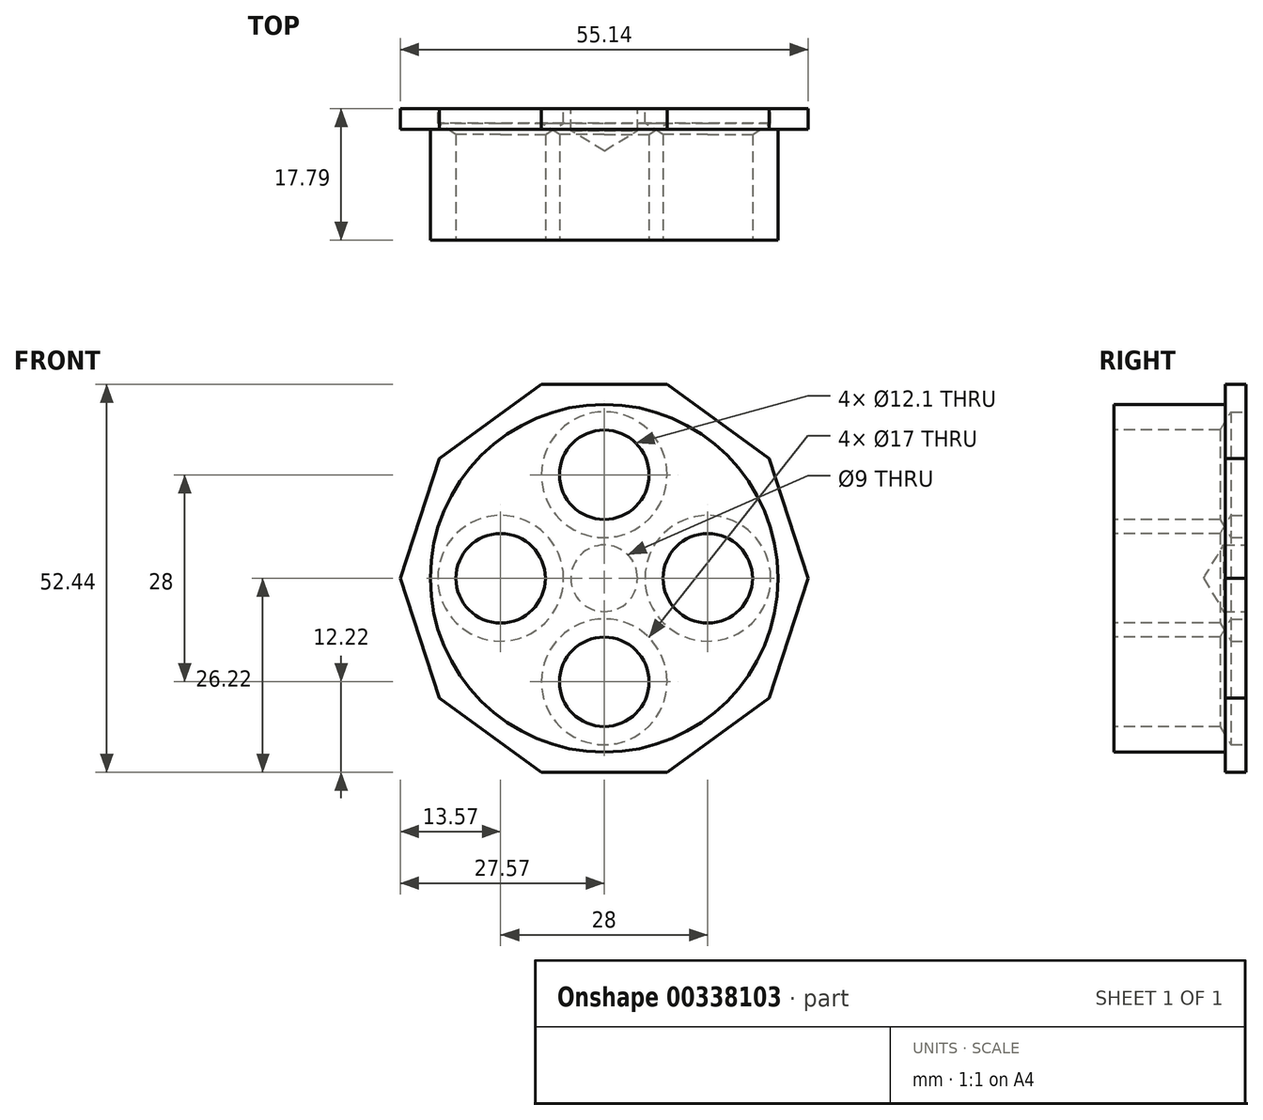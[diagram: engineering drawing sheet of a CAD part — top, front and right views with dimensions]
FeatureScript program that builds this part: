
annotation { "Feature Type Name" : "Feature", "Feature Type Description" : "" }
export const myFeature = defineFeature(function(context is Context, id is Id, definition is map)
    precondition{}
    {
        {
            var Q0;
            Q0=qCreatedBy(makeId("Front.planeOp"),FACE);
            var sketch = newSketch(context, id + "F0", { "sketchPlane" : qUnion([Q0])});
            skCircle(sketch, "E0.cCircle", {"center": v(0, 0) * mm, "radius": 27.57 * mm, "construction": true});
            skLineSegment(sketch, "E0.0", {"start": v(-27.57, 0) * mm, "end": v(-22.3, 16.2) * mm});
            skLineSegment(sketch, "E0.1", {"start": v(-22.3, 16.2) * mm, "end": v(-8.52, 26.22) * mm});
            skLineSegment(sketch, "E0.2", {"start": v(-8.52, 26.22) * mm, "end": v(8.52, 26.22) * mm});
            skLineSegment(sketch, "E0.3", {"start": v(8.52, 26.22) * mm, "end": v(22.3, 16.2) * mm});
            skLineSegment(sketch, "E0.4", {"start": v(22.3, 16.2) * mm, "end": v(27.57, 0) * mm});
            skLineSegment(sketch, "E0.5", {"start": v(27.57, 0) * mm, "end": v(22.3, -16.2) * mm});
            skLineSegment(sketch, "E0.6", {"start": v(22.3, -16.2) * mm, "end": v(8.52, -26.22) * mm});
            skLineSegment(sketch, "E0.7", {"start": v(8.52, -26.22) * mm, "end": v(-8.52, -26.22) * mm});
            skLineSegment(sketch, "E0.8", {"start": v(-8.52, -26.22) * mm, "end": v(-22.3, -16.2) * mm});
            skLineSegment(sketch, "E0.9", {"start": v(-22.3, -16.2) * mm, "end": v(-27.57, 0) * mm});
            skSolve(sketch);
        }
        {
            var Q0;
            Q0=makeQuery(id+"F0.imprint","IMPRINT",FACE,{"disambiguationData":[TD([[makeQuery(id+"F0.imprint","IMPRINT",EDGE,{"derivedFrom":sQuery(id+"F0.wireOp",EDGE,"E0.0")}),-1.0]])]});
            extrude(context, id + "F1", {"entities" : qUnion([Q0]), "depth" : 2.8 * mm});
        }
        {
            var Q0;
            Q0=makeQuery(id+"F1.opExtrude","CAP_FACE",FACE,{"disambiguationData":[OSD([sQuery(id+"F0.wireOp",EDGE,"E0.0"),sQuery(id+"F0.wireOp",EDGE,"E0.1"),sQuery(id+"F0.wireOp",EDGE,"E0.2"),sQuery(id+"F0.wireOp",EDGE,"E0.3"),sQuery(id+"F0.wireOp",EDGE,"E0.4"),sQuery(id+"F0.wireOp",EDGE,"E0.5"),sQuery(id+"F0.wireOp",EDGE,"E0.6"),sQuery(id+"F0.wireOp",EDGE,"E0.7"),sQuery(id+"F0.wireOp",EDGE,"E0.8"),sQuery(id+"F0.wireOp",EDGE,"E0.9")])],"isStart":false});
            var sketch = newSketch(context, id + "F2", { "sketchPlane" : qUnion([Q0])});
            skCircle(sketch, "E1", {"center": v(0, 0) * mm, "radius": 23.5 * mm});
            skSolve(sketch);
        }
        {
            var Q0;
            Q0=makeQuery(id+"F2.imprint","IMPRINT",FACE,{"disambiguationData":[TD([[makeQuery(id+"F2.imprint","IMPRINT",EDGE,{"derivedFrom":sQuery(id+"F2.wireOp",EDGE,"E1")}),1.0]])]});
            extrude(context, id + "F3", {"entities" : qUnion([Q0]), "operationType" : NewBodyOperationType.ADD, "depth" : 15 * mm});
        }
        {
            var Q0;
            Q0=makeQuery(id+"F3.opExtrude","CAP_FACE",FACE,{"disambiguationData":[OSD([sQuery(id+"F2.wireOp",EDGE,"E1")])],"isStart":false});
            var sketch = newSketch(context, id + "F4", { "sketchPlane" : qUnion([Q0])});
            skCircle(sketch, "E2", {"center": v(0, 14) * mm, "radius": 7 * mm});
            skCircle(sketch, "E3", {"center": v(14, 0) * mm, "radius": 7 * mm});
            skCircle(sketch, "E4", {"center": v(0, -14) * mm, "radius": 7 * mm});
            skCircle(sketch, "E5", {"center": v(-14, 0) * mm, "radius": 7 * mm});
            skSolve(sketch);
        }
        {
            var Q0;
            Q0=sQuery(id+"F4.wireOp",VERTEX,"E5.center");
            var Q1;
            Q1=sQuery(id+"F4.wireOp",VERTEX,"E2.center");
            var Q2;
            Q2=sQuery(id+"F4.wireOp",VERTEX,"E3.center");
            var Q3;
            Q3=sQuery(id+"F4.wireOp",VERTEX,"E4.center");
            var Q4;
            Q4=makeQuery(id+"F1.opExtrude","SWEPT_BODY",BODY,{"disambiguationData":[OSD([sQuery(id+"F0.wireOp",EDGE,"E0.0"),sQuery(id+"F0.wireOp",EDGE,"E0.1"),sQuery(id+"F0.wireOp",EDGE,"E0.2"),sQuery(id+"F0.wireOp",EDGE,"E0.3"),sQuery(id+"F0.wireOp",EDGE,"E0.4"),sQuery(id+"F0.wireOp",EDGE,"E0.5"),sQuery(id+"F0.wireOp",EDGE,"E0.6"),sQuery(id+"F0.wireOp",EDGE,"E0.7"),sQuery(id+"F0.wireOp",EDGE,"E0.8"),sQuery(id+"F0.wireOp",EDGE,"E0.9")])]});
            hole(context, id + "F5", {"style" : HoleStyle.SIMPLE, "endStyle" : HoleEndStyle.THROUGH, "standardTappedOrClearance" : lookupTablePath({ "standard" : "ISO", "engagement" : "75%", "pitch" : "2 mm", "size" : "M14", "type" : "Tapped" }), "standardBlindInLast" : lookupTablePath({ "standard" : "ISO", "engagement" : "75%", "pitch" : "2 mm", "size" : "M14", "type" : "Tapped" }), "holeDiameter" : 12.1 * mm, "showTappedDepth" : true, "tappedDepth" : 12 * mm, "tapClearance" : 3, "locations" : qUnion([Q0, Q1, Q2, Q3]), "scope" : qUnion([Q4]), "majorDiameter" : 14 * mm});
        }
        {
            var Q0;
            Q0=makeQuery(id+"F1.opExtrude","CAP_FACE",FACE,{"disambiguationData":[OSD([sQuery(id+"F0.wireOp",EDGE,"E0.0"),sQuery(id+"F0.wireOp",EDGE,"E0.1"),sQuery(id+"F0.wireOp",EDGE,"E0.2"),sQuery(id+"F0.wireOp",EDGE,"E0.3"),sQuery(id+"F0.wireOp",EDGE,"E0.4"),sQuery(id+"F0.wireOp",EDGE,"E0.5"),sQuery(id+"F0.wireOp",EDGE,"E0.6"),sQuery(id+"F0.wireOp",EDGE,"E0.7"),sQuery(id+"F0.wireOp",EDGE,"E0.8"),sQuery(id+"F0.wireOp",EDGE,"E0.9")])],"isStart":true});
            var sketch = newSketch(context, id + "F6", { "sketchPlane" : qUnion([Q0])});
            skCircle(sketch, "E6", {"center": v(0, 0) * mm, "radius": 4.5 * mm});
            skSolve(sketch);
        }
        {
            var Q0;
            Q0=sQuery(id+"F6.wireOp",VERTEX,"E6.center");
            var Q1;
            Q1=makeQuery(id+"F1.opExtrude","SWEPT_BODY",BODY,{"disambiguationData":[OSD([sQuery(id+"F0.wireOp",EDGE,"E0.0"),sQuery(id+"F0.wireOp",EDGE,"E0.1"),sQuery(id+"F0.wireOp",EDGE,"E0.2"),sQuery(id+"F0.wireOp",EDGE,"E0.3"),sQuery(id+"F0.wireOp",EDGE,"E0.4"),sQuery(id+"F0.wireOp",EDGE,"E0.5"),sQuery(id+"F0.wireOp",EDGE,"E0.6"),sQuery(id+"F0.wireOp",EDGE,"E0.7"),sQuery(id+"F0.wireOp",EDGE,"E0.8"),sQuery(id+"F0.wireOp",EDGE,"E0.9")])]});
            hole(context, id + "F7", {"style" : HoleStyle.SIMPLE, "endStyle" : HoleEndStyle.BLIND, "holeDiameter" : 9 * mm, "holeDepth" : 3 * mm, "tappedDepth" : 12 * mm, "tapClearance" : 3, "locations" : qUnion([Q0]), "scope" : qUnion([Q1])});
        }
        {
            var Q0;
            Q0=makeQuery(id+"F1.opExtrude","CAP_FACE",FACE,{"disambiguationData":[OSD([sQuery(id+"F0.wireOp",EDGE,"E0.0"),sQuery(id+"F0.wireOp",EDGE,"E0.1"),sQuery(id+"F0.wireOp",EDGE,"E0.2"),sQuery(id+"F0.wireOp",EDGE,"E0.3"),sQuery(id+"F0.wireOp",EDGE,"E0.4"),sQuery(id+"F0.wireOp",EDGE,"E0.5"),sQuery(id+"F0.wireOp",EDGE,"E0.6"),sQuery(id+"F0.wireOp",EDGE,"E0.7"),sQuery(id+"F0.wireOp",EDGE,"E0.8"),sQuery(id+"F0.wireOp",EDGE,"E0.9")])],"isStart":true});
            var sketch = newSketch(context, id + "F8", { "sketchPlane" : qUnion([Q0])});
            skCircle(sketch, "E7", {"center": v(-14, 0) * mm, "radius": 8.5 * mm});
            skCircle(sketch, "E8", {"center": v(0, 14) * mm, "radius": 8.5 * mm});
            skCircle(sketch, "E9", {"center": v(14, 0) * mm, "radius": 8.5 * mm});
            skCircle(sketch, "E10", {"center": v(0, -14) * mm, "radius": 8.5 * mm});
            skSolve(sketch);
        }
        {
            var Q0;
            Q0=sQuery(id+"F8.wireOp",VERTEX,"E7.center");
            var Q1;
            Q1=sQuery(id+"F8.wireOp",VERTEX,"E8.center");
            var Q2;
            Q2=sQuery(id+"F8.wireOp",VERTEX,"E9.center");
            var Q3;
            Q3=sQuery(id+"F8.wireOp",VERTEX,"E10.center");
            var Q4;
            Q4=makeQuery(id+"F1.opExtrude","SWEPT_BODY",BODY,{"disambiguationData":[OSD([sQuery(id+"F0.wireOp",EDGE,"E0.0"),sQuery(id+"F0.wireOp",EDGE,"E0.1"),sQuery(id+"F0.wireOp",EDGE,"E0.2"),sQuery(id+"F0.wireOp",EDGE,"E0.3"),sQuery(id+"F0.wireOp",EDGE,"E0.4"),sQuery(id+"F0.wireOp",EDGE,"E0.5"),sQuery(id+"F0.wireOp",EDGE,"E0.6"),sQuery(id+"F0.wireOp",EDGE,"E0.7"),sQuery(id+"F0.wireOp",EDGE,"E0.8"),sQuery(id+"F0.wireOp",EDGE,"E0.9")])]});
            hole(context, id + "F9", {"style" : HoleStyle.SIMPLE, "endStyle" : HoleEndStyle.BLIND, "holeDiameter" : 17 * mm, "holeDepth" : 2 * mm, "tappedDepth" : 12 * mm, "tapClearance" : 3, "locations" : qUnion([Q0, Q1, Q2, Q3]), "scope" : qUnion([Q4])});
        }
    });
